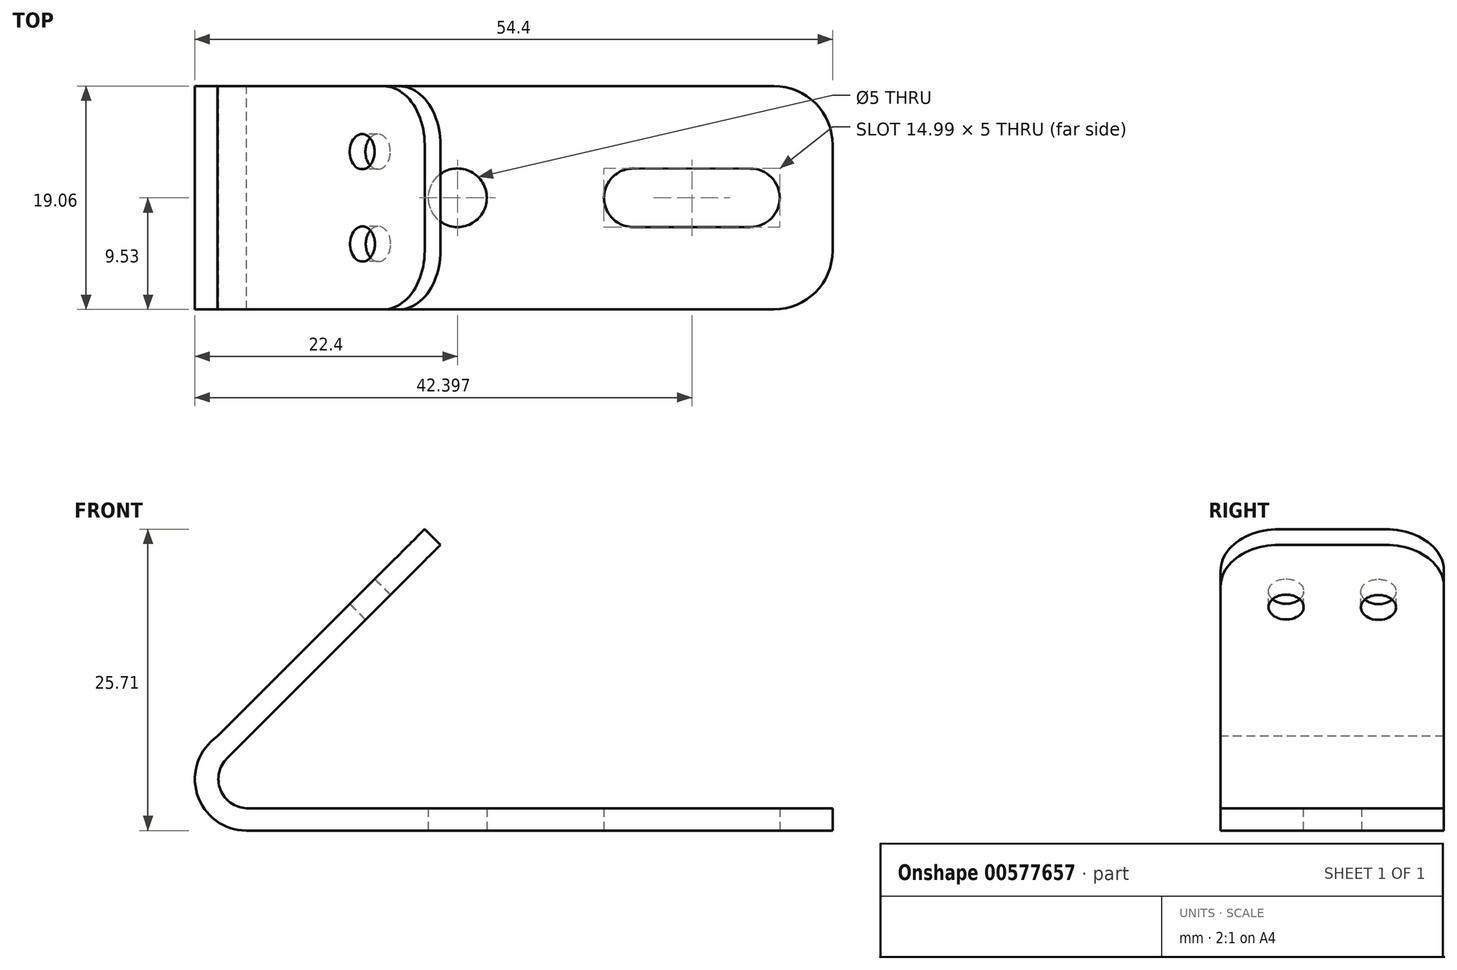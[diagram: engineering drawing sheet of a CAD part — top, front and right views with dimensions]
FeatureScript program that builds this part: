
annotation { "Feature Type Name" : "Feature", "Feature Type Description" : "" }
export const myFeature = defineFeature(function(context is Context, id is Id, definition is map)
    precondition{}
    {
        {
            var Q0;
            Q0=qCreatedBy(makeId("Top.planeOp"),FACE);
            var sketch = newSketch(context, id + "F0", { "sketchPlane" : qUnion([Q0])});
            skCircle(sketch, "E0", {"center": v(0, 0) * mm, "radius": 2.5 * mm});
            skLineSegment(sketch, "E1", {"start": v(32, 9.53) * mm, "end": v(32, -9.53) * mm});
            skLineSegment(sketch, "E2", {"start": v(32, -9.53) * mm, "end": v(-18, -9.53) * mm});
            skLineSegment(sketch, "E3", {"start": v(-18, -9.53) * mm, "end": v(-18, 9.53) * mm});
            skLineSegment(sketch, "E4", {"start": v(-18, 9.53) * mm, "end": v(32, 9.53) * mm});
            skPoint(sketch, "E5.endSnap0", {"position": v(32, 0) * mm});
            skCircle(sketch, "E6", {"center": v(25, 0) * mm, "radius": 2.5 * mm});
            skCircle(sketch, "E7", {"center": v(15, 0) * mm, "radius": 2.5 * mm});
            skLineSegment(sketch, "E8", {"start": v(15, 2.5) * mm, "end": v(25, 2.5) * mm});
            skLineSegment(sketch, "E9", {"start": v(25, -2.5) * mm, "end": v(15, -2.5) * mm});
            skSolve(sketch);
        }
        {
            var Q0;
            Q0=makeQuery(id+"F0.imprint","IMPRINT",FACE,{"disambiguationData":[TD([[makeQuery(id+"F0.imprint","IMPRINT",EDGE,{"derivedFrom":sQuery(id+"F0.wireOp",EDGE,"E0")}),-1.0]])]});
            extrude(context, id + "F1", {"entities" : qUnion([Q0]), "depth" : 1.9 * mm, "offsetDistance" : 25.4 * mm});
        }
        {
            var Q0;
            Q0=makeQuery(id+"F1.opExtrude","SWEPT_EDGE",EDGE,{"disambiguationData":[OSD([sQuery(id+"F0.wireOp",EDGE,"E1"),sQuery(id+"F0.wireOp",EDGE,"E2")])]});
            var Q1;
            Q1=makeQuery(id+"F1.opExtrude","SWEPT_EDGE",EDGE,{"disambiguationData":[OSD([sQuery(id+"F0.wireOp",EDGE,"E1"),sQuery(id+"F0.wireOp",EDGE,"E4")])]});
            fillet(context, id + "F2", {"entities" : qUnion([Q0, Q1]), "radius" : 5 * mm, "tangentPropagation" : true, "allowEdgeOverflow" : false});
        }
        {
            var Q0;
            Q0=makeQuery(id+"F1.opExtrude","SWEPT_FACE",FACE,{"disambiguationData":[OSD([sQuery(id+"F0.wireOp",EDGE,"E2")])]});
            var sketch = newSketch(context, id + "F3", { "sketchPlane" : qUnion([Q0])});
            skArc(sketch, "E10", {"start": v(-20.48, 8.04) * mm, "mid": v(-22.2, 3.1) * mm, "end": v(-18, 0) * mm});
            skLineSegment(sketch, "E11", {"start": v(-20.48, 8.04) * mm, "end": v(-2.8, 25.71) * mm});
            skLineSegment(sketch, "E12", {"start": v(-2.8, 25.71) * mm, "end": v(-1.45, 24.37) * mm});
            skLineSegment(sketch, "E13", {"start": v(-1.45, 24.37) * mm, "end": v(-19.66, 6.17) * mm});
            skArc(sketch, "E14", {"start": v(-19.66, 6.17) * mm, "mid": v(-20.22, 3.5) * mm, "end": v(-18, 1.9) * mm});
            skSolve(sketch);
        }
        {
            var Q0;
            Q0=makeQuery(id+"F3.imprint","IMPRINT",FACE,{"disambiguationData":[TD([[makeQuery(id+"F3.imprint","IMPRINT",EDGE,{"derivedFrom":sQuery(id+"F3.wireOp",EDGE,"E10")}),1.0]])]});
            extrude(context, id + "F4", {"entities" : qUnion([Q0]), "operationType" : NewBodyOperationType.ADD, "oppositeDirection" : true, "depth" : 19.05 * mm, "offsetDistance" : 25 * mm});
        }
        {
            var Q0;
            Q0=makeQuery(id+"F4.opExtrude","CAP_EDGE",EDGE,{"disambiguationData":[OSD([sQuery(id+"F3.wireOp",EDGE,"E12")])],"isStart":true});
            var Q1;
            Q1=makeQuery(id+"F4.opExtrude","CAP_EDGE",EDGE,{"disambiguationData":[OSD([sQuery(id+"F3.wireOp",EDGE,"E12")])],"isStart":false});
            fillet(context, id + "F5", {"entities" : qUnion([Q0, Q1]), "radius" : 5 * mm, "tangentPropagation" : true, "allowEdgeOverflow" : false});
        }
        {
            var Q0;
            Q0=makeQuery(id+"F4.opExtrude","SWEPT_FACE",FACE,{"disambiguationData":[OSD([sQuery(id+"F3.wireOp",EDGE,"E11")])]});
            var sketch = newSketch(context, id + "F6", { "sketchPlane" : qUnion([Q0])});
            skCircle(sketch, "E15", {"center": v(-3.94, 8.66) * mm, "radius": 1.5 * mm});
            skCircle(sketch, "E16", {"center": v(3.94, 8.7) * mm, "radius": 1.5 * mm});
            skSolve(sketch);
        }
        {
            var Q0;
            Q0=makeQuery(id+"F6.imprint","IMPRINT",FACE,{"disambiguationData":[TD([[makeQuery(id+"F6.imprint","IMPRINT",EDGE,{"derivedFrom":sQuery(id+"F6.wireOp",EDGE,"E15")}),1.0]])]});
            var Q1;
            Q1=makeQuery(id+"F6.imprint","IMPRINT",FACE,{"disambiguationData":[TD([[makeQuery(id+"F6.imprint","IMPRINT",EDGE,{"derivedFrom":sQuery(id+"F6.wireOp",EDGE,"E16")}),1.0]])]});
            extrude(context, id + "F7", {"entities" : qUnion([Q0, Q1]), "operationType" : NewBodyOperationType.REMOVE, "oppositeDirection" : true, "depth" : 5 * mm, "offsetDistance" : 25 * mm});
        }
    });
